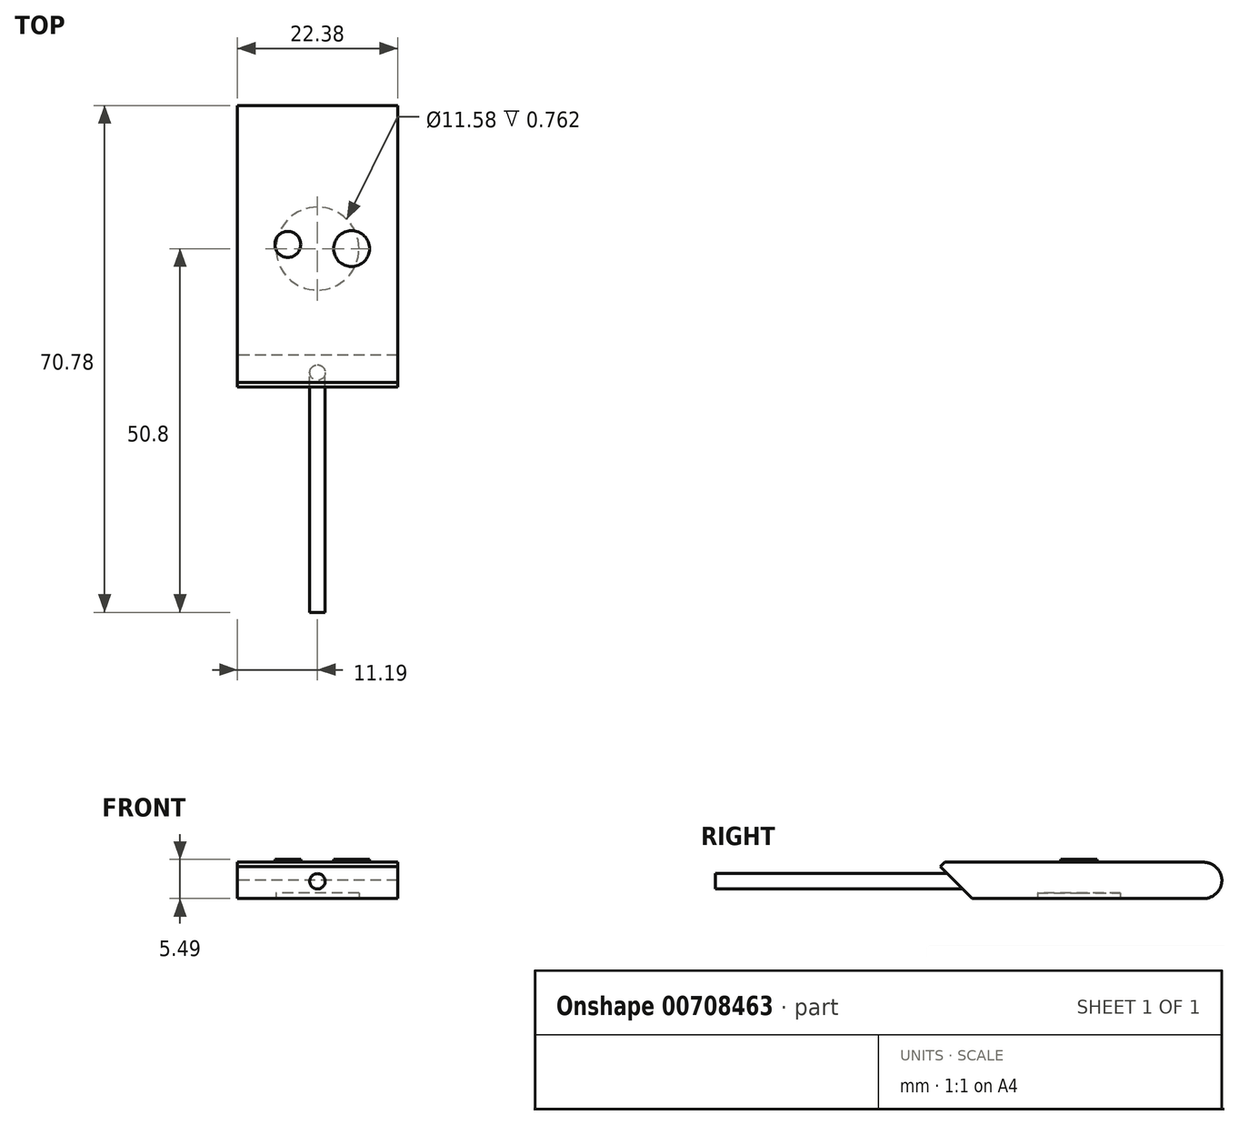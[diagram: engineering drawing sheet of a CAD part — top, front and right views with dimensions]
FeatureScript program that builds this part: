
annotation { "Feature Type Name" : "Feature", "Feature Type Description" : "" }
export const myFeature = defineFeature(function(context is Context, id is Id, definition is map)
    precondition{}
    {
        {
            var Q0;
            Q0=qCreatedBy(makeId("Top.planeOp"),FACE);
            var sketch = newSketch(context, id + "F0", { "sketchPlane" : qUnion([Q0])});
            skLineSegment(sketch, "E0.bottom", {"start": v(11.19, -19.99) * mm, "end": v(-11.19, -19.99) * mm});
            skLineSegment(sketch, "E0.top", {"start": v(11.19, 19.99) * mm, "end": v(-11.19, 19.99) * mm});
            skLineSegment(sketch, "E0.left", {"start": v(11.19, -19.99) * mm, "end": v(11.19, 19.99) * mm});
            skLineSegment(sketch, "E0.right", {"start": v(-11.19, -19.99) * mm, "end": v(-11.19, 19.99) * mm});
            skPoint(sketch, "E0.middle", {"position": v(0, 0) * mm});
            skSolve(sketch);
        }
        {
            var Q0;
            Q0=makeQuery(id+"F0.imprint","IMPRINT",FACE,{"disambiguationData":[TD([[makeQuery(id+"F0.imprint","IMPRINT",EDGE,{"derivedFrom":sQuery(id+"F0.wireOp",EDGE,"E0.bottom")}),-1.0]])]});
            extrude(context, id + "F1", {"entities" : qUnion([Q0]), "depth" : 5.08 * mm, "offsetDistance" : 25.4 * mm});
        }
        {
            var Q0;
            Q0=qCreatedBy(makeId("Top.planeOp"),FACE);
            var sketch = newSketch(context, id + "F2", { "sketchPlane" : qUnion([Q0])});
            skCircle(sketch, "E1", {"center": v(0, 0) * mm, "radius": 5.8 * mm});
            skSolve(sketch);
        }
        {
            var Q0;
            Q0=makeQuery(id+"F2.imprint","IMPRINT",FACE,{"disambiguationData":[TD([[makeQuery(id+"F2.imprint","IMPRINT",EDGE,{"derivedFrom":sQuery(id+"F2.wireOp",EDGE,"E1")}),1.0]])]});
            var Q1;
            Q1=sQuery(id+"F2.wireOp",EDGE,"E1");
            extrude(context, id + "F3", {"entities" : qUnion([Q0]), "operationType" : NewBodyOperationType.REMOVE, "surfaceEntities" : qUnion([Q1]), "depth" : 0.76 * mm, "offsetDistance" : 25.4 * mm});
        }
        {
            var Q0;
            Q0=qCreatedBy(makeId("Front.planeOp"),FACE);
            var sketch = newSketch(context, id + "F4", { "sketchPlane" : qUnion([Q0])});
            skCircle(sketch, "E2", {"center": v(0, 2.4) * mm, "radius": 1.08 * mm});
            skSolve(sketch);
        }
        {
            var Q0;
            Q0=qSketchRegion(id+"F4",true);
            extrude(context, id + "F5", {"entities" : qUnion([Q0]), "operationType" : NewBodyOperationType.ADD, "depth" : 50.8 * mm, "offsetDistance" : 25.4 * mm});
        }
        {
            var Q0;
            Q0=makeQuery(id+"F1.opExtrude","CAP_FACE",FACE,{"disambiguationData":[OSD([sQuery(id+"F0.wireOp",EDGE,"E0.bottom"),sQuery(id+"F0.wireOp",EDGE,"E0.top"),sQuery(id+"F0.wireOp",EDGE,"E0.left"),sQuery(id+"F0.wireOp",EDGE,"E0.right")])],"isStart":false});
            var sketch = newSketch(context, id + "F6", { "sketchPlane" : qUnion([Q0])});
            skCircle(sketch, "E3", {"center": v(4.77, 0) * mm, "radius": 2.51 * mm});
            skCircle(sketch, "E4", {"center": v(-4.15, 0.58) * mm, "radius": 1.81 * mm});
            skSolve(sketch);
        }
        {
            var Q0;
            Q0=makeQuery(id+"F6.imprint","IMPRINT",FACE,{"disambiguationData":[TD([[makeQuery(id+"F6.imprint","IMPRINT",EDGE,{"derivedFrom":sQuery(id+"F6.wireOp",EDGE,"E4")}),1.0]])]});
            var Q1;
            Q1=makeQuery(id+"F6.imprint","IMPRINT",FACE,{"disambiguationData":[TD([[makeQuery(id+"F6.imprint","IMPRINT",EDGE,{"derivedFrom":sQuery(id+"F6.wireOp",EDGE,"E3")}),1.0]])]});
            extrude(context, id + "F7", {"entities" : qUnion([Q0, Q1]), "operationType" : NewBodyOperationType.ADD, "depth" : 0.4 * mm, "offsetDistance" : 25.4 * mm});
        }
        {
            var Q0;
            Q0=makeQuery(id+"F1.opExtrude","CAP_EDGE",EDGE,{"disambiguationData":[OSD([sQuery(id+"F0.wireOp",EDGE,"E0.bottom")])],"isStart":false});
            chamfer(context, id + "F8", {"entities" : qUnion([Q0]), "width" : 1.27 * mm, "tangentPropagation" : true});
        }
        {
            var Q0;
            Q0=makeQuery(id+"F1.opExtrude","CAP_EDGE",EDGE,{"disambiguationData":[OSD([sQuery(id+"F0.wireOp",EDGE,"E0.bottom")])],"isStart":true});
            chamfer(context, id + "F9", {"entities" : qUnion([Q0]), "width" : 5.08 * mm, "tangentPropagation" : true});
        }
        {
            var Q0;
            Q0=makeQuery(id+"F1.opExtrude","CAP_EDGE",EDGE,{"disambiguationData":[OSD([sQuery(id+"F0.wireOp",EDGE,"E0.top")])],"isStart":false});
            var Q1;
            Q1=makeQuery(id+"F1.opExtrude","CAP_EDGE",EDGE,{"disambiguationData":[OSD([sQuery(id+"F0.wireOp",EDGE,"E0.top")])],"isStart":true});
            chamfer(context, id + "F10", {"entities" : qUnion([Q0, Q1]), "width" : 1.52 * mm, "tangentPropagation" : true});
        }
        {
            var Q0;
            {var subQ0=sQuery(id+"F0.wireOp",EDGE,"E0.top");Q0=makeQuery(id+"F10.opChamfer","BLEND_EDGE",EDGE,{"blendedFrom":[makeQuery(id+"F1.opExtrude","CAP_EDGE",EDGE,{"disambiguationData":[OSD([subQ0])],"isStart":false}),makeQuery(id+"F1.opExtrude","CAP_FACE",FACE,{"disambiguationData":[OSD([sQuery(id+"F0.wireOp",EDGE,"E0.bottom"),subQ0,sQuery(id+"F0.wireOp",EDGE,"E0.left"),sQuery(id+"F0.wireOp",EDGE,"E0.right")])],"isStart":false})],"blendedInto":[makeQuery(id+"F1.opExtrude","CAP_FACE",FACE,{"disambiguationData":[OSD([sQuery(id+"F0.wireOp",EDGE,"E0.bottom"),subQ0,sQuery(id+"F0.wireOp",EDGE,"E0.left"),sQuery(id+"F0.wireOp",EDGE,"E0.right")])],"isStart":false})]});}
            var Q1;
            {var subQ0=sQuery(id+"F0.wireOp",EDGE,"E0.top");Q1=makeQuery(id+"F10.opChamfer","BLEND_EDGE",EDGE,{"blendedFrom":[makeQuery(id+"F1.opExtrude","CAP_EDGE",EDGE,{"disambiguationData":[OSD([subQ0])],"isStart":false}),makeQuery(id+"F1.opExtrude","SWEPT_FACE",FACE,{"disambiguationData":[OSD([subQ0])]})],"blendedInto":[makeQuery(id+"F1.opExtrude","SWEPT_FACE",FACE,{"disambiguationData":[OSD([subQ0])]})]});}
            var Q2;
            {var subQ0=sQuery(id+"F0.wireOp",EDGE,"E0.top");Q2=makeQuery(id+"F10.opChamfer","BLEND_EDGE",EDGE,{"blendedFrom":[makeQuery(id+"F1.opExtrude","CAP_EDGE",EDGE,{"disambiguationData":[OSD([subQ0])],"isStart":true}),makeQuery(id+"F1.opExtrude","SWEPT_FACE",FACE,{"disambiguationData":[OSD([subQ0])]})],"blendedInto":[makeQuery(id+"F1.opExtrude","SWEPT_FACE",FACE,{"disambiguationData":[OSD([subQ0])]})]});}
            var Q3;
            {var subQ0=sQuery(id+"F0.wireOp",EDGE,"E0.top");Q3=makeQuery(id+"F10.opChamfer","BLEND_EDGE",EDGE,{"blendedFrom":[makeQuery(id+"F1.opExtrude","CAP_EDGE",EDGE,{"disambiguationData":[OSD([subQ0])],"isStart":true}),makeQuery(id+"F1.opExtrude","CAP_FACE",FACE,{"disambiguationData":[OSD([sQuery(id+"F0.wireOp",EDGE,"E0.bottom"),subQ0,sQuery(id+"F0.wireOp",EDGE,"E0.left"),sQuery(id+"F0.wireOp",EDGE,"E0.right")])],"isStart":true})],"blendedInto":[makeQuery(id+"F1.opExtrude","CAP_FACE",FACE,{"disambiguationData":[OSD([sQuery(id+"F0.wireOp",EDGE,"E0.bottom"),subQ0,sQuery(id+"F0.wireOp",EDGE,"E0.left"),sQuery(id+"F0.wireOp",EDGE,"E0.right")])],"isStart":true})]});}
            fillet(context, id + "F11", {"entities" : qUnion([Q0, Q1, Q2, Q3]), "radius" : 2.54 * mm, "tangentPropagation" : true, "allowEdgeOverflow" : false});
        }
    });
